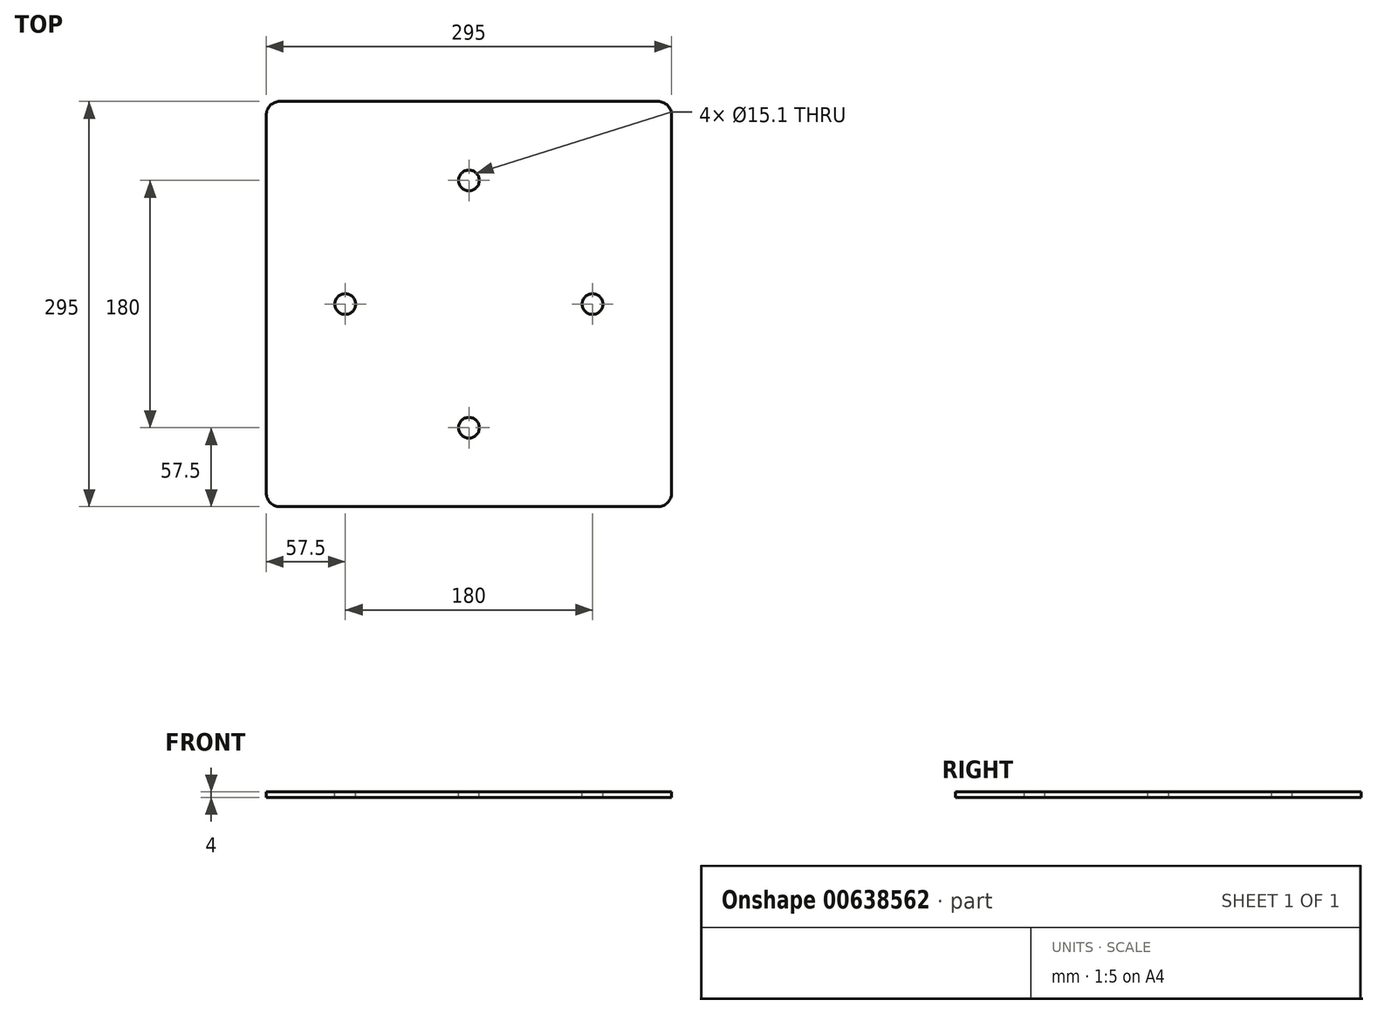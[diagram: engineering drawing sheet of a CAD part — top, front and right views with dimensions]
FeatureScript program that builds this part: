
annotation { "Feature Type Name" : "Feature", "Feature Type Description" : "" }
export const myFeature = defineFeature(function(context is Context, id is Id, definition is map)
    precondition{}
    {
        {
            var Q0;
            Q0=qCreatedBy(makeId("Top.planeOp"),FACE);
            var sketch = newSketch(context, id + "F0", { "sketchPlane" : qUnion([Q0])});
            skLineSegment(sketch, "E0.bottom", {"start": v(-137.5, 147.5) * mm, "end": v(137.5, 147.5) * mm});
            skLineSegment(sketch, "E0.top", {"start": v(-137.5, -147.5) * mm, "end": v(137.5, -147.5) * mm});
            skLineSegment(sketch, "E0.left", {"start": v(-147.5, 137.5) * mm, "end": v(-147.5, -137.5) * mm});
            skLineSegment(sketch, "E0.right", {"start": v(147.5, 137.5) * mm, "end": v(147.5, -137.5) * mm});
            skPoint(sketch, "E0.middle", {"position": v(0, 0) * mm});
            skCircle(sketch, "E1", {"center": v(0, 0) * mm, "radius": 90 * mm, "construction": true});
            skCircle(sketch, "E2", {"center": v(0, 90) * mm, "radius": 5 * mm});
            skCircle(sketch, "E3.1.0", {"center": v(-90, 0) * mm, "radius": 5 * mm});
            skCircle(sketch, "E3.2.0", {"center": v(0, -90) * mm, "radius": 5 * mm});
            skCircle(sketch, "E3.3.0", {"center": v(90, 0) * mm, "radius": 5 * mm});
            skPoint(sketch, "E4.visualSharp", {"position": v(-147.5, 147.5) * mm});
            skArc(sketch, "E4.filletArc", {"start": v(-137.5, 147.5) * mm, "mid": v(-144.57, 144.57) * mm, "end": v(-147.5, 137.5) * mm});
            skPoint(sketch, "E5.visualSharp", {"position": v(147.5, 147.5) * mm});
            skArc(sketch, "E5.filletArc", {"start": v(147.5, 137.5) * mm, "mid": v(144.57, 144.57) * mm, "end": v(137.5, 147.5) * mm});
            skPoint(sketch, "E6.visualSharp", {"position": v(147.5, -147.5) * mm});
            skArc(sketch, "E6.filletArc", {"start": v(137.5, -147.5) * mm, "mid": v(144.57, -144.57) * mm, "end": v(147.5, -137.5) * mm});
            skPoint(sketch, "E7.visualSharp", {"position": v(-147.5, -147.5) * mm});
            skArc(sketch, "E7.filletArc", {"start": v(-147.5, -137.5) * mm, "mid": v(-144.57, -144.57) * mm, "end": v(-137.5, -147.5) * mm});
            skSolve(sketch);
        }
        {
            var Q0;
            Q0=qSketchRegion(id+"F0",true);
            extrude(context, id + "F1", {"entities" : qUnion([Q0]), "depth" : 4 * mm, "offsetDistance" : 25 * mm});
        }
        {
            var Q0;
            Q0=makeQuery(id+"F1.opExtrude","CAP_FACE",FACE,{"disambiguationData":[OSD([sQuery(id+"F0.wireOp",EDGE,"E0.bottom"),sQuery(id+"F0.wireOp",EDGE,"E0.top"),sQuery(id+"F0.wireOp",EDGE,"E0.left"),sQuery(id+"F0.wireOp",EDGE,"E0.right"),sQuery(id+"F0.wireOp",EDGE,"m58s0BAB-fvvz-2rnM-DKYV-08GH9UUX4HQB"),sQuery(id+"F0.wireOp",EDGE,"E2"),sQuery(id+"F0.wireOp",EDGE,"E3.1.0"),sQuery(id+"F0.wireOp",EDGE,"E3.2.0"),sQuery(id+"F0.wireOp",EDGE,"E3.3.0"),sQuery(id+"F0.wireOp",EDGE,"E4.filletArc"),sQuery(id+"F0.wireOp",EDGE,"E5.filletArc"),sQuery(id+"F0.wireOp",EDGE,"E6.filletArc"),sQuery(id+"F0.wireOp",EDGE,"E7.filletArc")])],"isStart":false});
            var sketch = newSketch(context, id + "F2", { "sketchPlane" : qUnion([Q0])});
            skCircle(sketch, "E8", {"center": v(0, 0) * mm, "radius": 90 * mm, "construction": true});
            skCircle(sketch, "E9", {"center": v(0, 90) * mm, "radius": 7.55 * mm});
            skCircle(sketch, "E10.1.0", {"center": v(-90, 0) * mm, "radius": 7.55 * mm});
            skCircle(sketch, "E10.2.0", {"center": v(0, -90) * mm, "radius": 7.55 * mm});
            skCircle(sketch, "E10.3.0", {"center": v(90, 0) * mm, "radius": 7.55 * mm});
            skSolve(sketch);
        }
        {
            var Q0;
            Q0=qSketchRegion(id+"F2",true);
            extrude(context, id + "F3", {"entities" : qUnion([Q0]), "operationType" : NewBodyOperationType.REMOVE, "oppositeDirection" : true, "depth" : 25 * mm, "offsetDistance" : 25 * mm});
        }
    });
